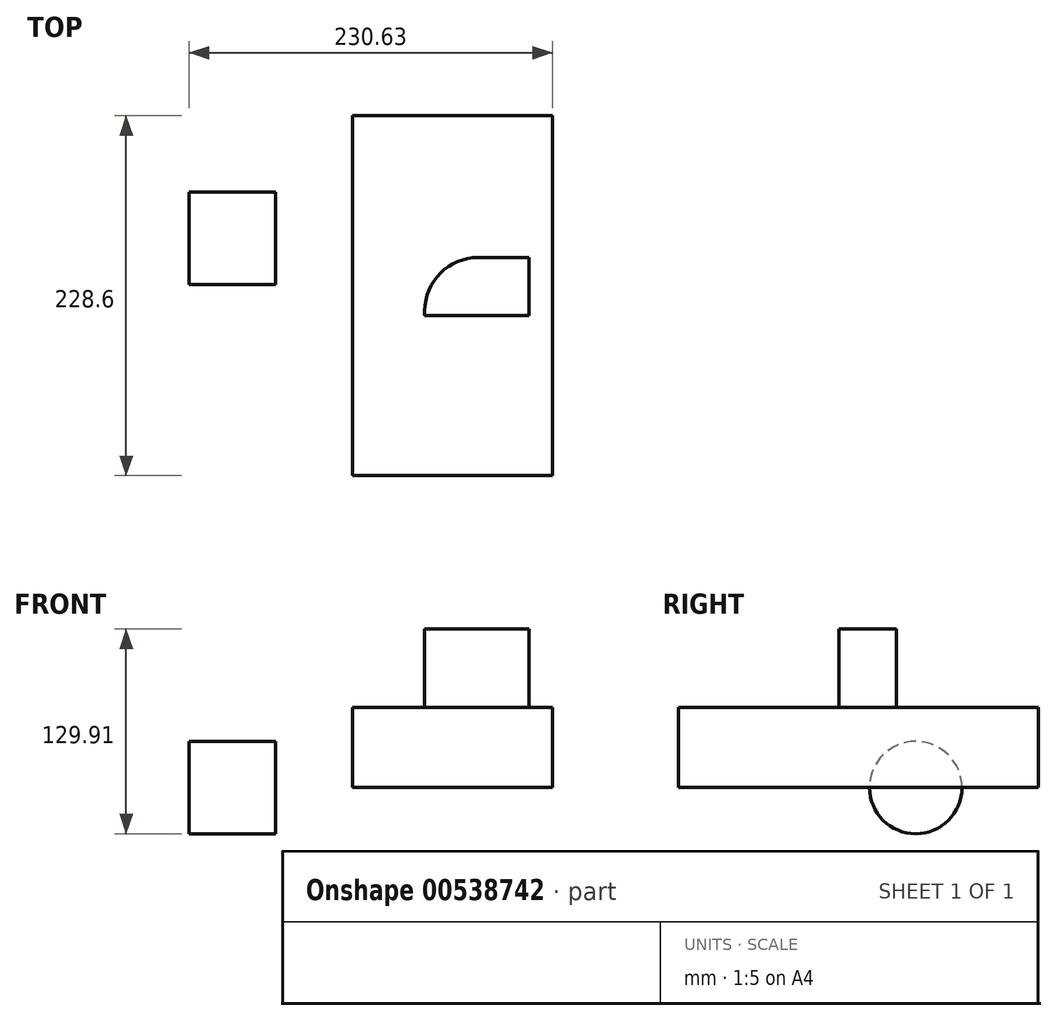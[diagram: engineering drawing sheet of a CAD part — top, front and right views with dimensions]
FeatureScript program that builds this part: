
annotation { "Feature Type Name" : "Feature", "Feature Type Description" : "" }
export const myFeature = defineFeature(function(context is Context, id is Id, definition is map)
    precondition{}
    {
        {
            var Q0;
            Q0=qCreatedBy(makeId("Top.planeOp"),FACE);
            var sketch = newSketch(context, id + "F0", { "sketchPlane" : qUnion([Q0])});
            skLineSegment(sketch, "E0.bottom", {"start": v(63.5, -114.3) * mm, "end": v(-63.5, -114.3) * mm});
            skLineSegment(sketch, "E0.top", {"start": v(63.5, 114.3) * mm, "end": v(-63.5, 114.3) * mm});
            skLineSegment(sketch, "E0.left", {"start": v(63.5, -114.3) * mm, "end": v(63.5, 114.3) * mm});
            skLineSegment(sketch, "E0.right", {"start": v(-63.5, -114.3) * mm, "end": v(-63.5, 114.3) * mm});
            skPoint(sketch, "E0.middle", {"position": v(0, 0) * mm});
            skSolve(sketch);
        }
        {
            var Q0;
            Q0 = qSketchRegion(id + "F0", true);
            extrude(context, id + "F1", {"entities" : qUnion([Q0]), "depth" : 50.8 * mm, "offsetDistance" : 25.4 * mm});
        }
        {
            var Q0;
            Q0=qCreatedBy(makeId("Top.planeOp"),FACE);
            var sketch = newSketch(context, id + "F2", { "sketchPlane" : qUnion([Q0])});
            skLineSegment(sketch, "E1.bottom", {"start": v(-141.73, 65.86) * mm, "end": v(-112.4, 65.86) * mm});
            skLineSegment(sketch, "E1.top", {"start": v(-141.73, 36.53) * mm, "end": v(-112.4, 36.53) * mm});
            skLineSegment(sketch, "E1.left", {"start": v(-141.73, 65.86) * mm, "end": v(-141.73, 36.53) * mm});
            skLineSegment(sketch, "E1.right", {"start": v(-112.4, 65.86) * mm, "end": v(-112.4, 36.53) * mm});
            skLineSegment(sketch, "E2", {"start": v(-141.73, 36.53) * mm, "end": v(-88.75, 36.53) * mm});
            skSolve(sketch);
        }
        {
            var Q0;
            Q0=makeQuery(id+"F2.imprint","IMPRINT",FACE,{"disambiguationData":[TD([[makeQuery(id+"F2.imprint","IMPRINT",EDGE,{"derivedFrom":sQuery(id+"F2.wireOp",EDGE,"E1.bottom")}),-1.0]])]});
            var Q1;
            Q1=sQuery(id+"F2.wireOp",EDGE,"E2");
            revolve(context, id + "F3", {"entities" : qUnion([Q0]), "axis" : qUnion([Q1]), "revolveType" : RevolveType.FULL});
        }
        {
            var Q0;
            Q0=makeQuery(id+"F3.opRevolve","SWEPT_FACE",FACE,{"disambiguationData":[OSD([sQuery(id+"F2.wireOp",EDGE,"E1.left")])]});
            extrude(context, id + "F4", {"entities" : qUnion([Q0]), "operationType" : NewBodyOperationType.ADD, "depth" : 25.4 * mm, "offsetDistance" : 25.4 * mm});
        }
        {
            var Q0;
            Q0=makeQuery(id+"F1.opExtrude","CAP_FACE",FACE,{"disambiguationData":[OSD([sQuery(id+"F0.wireOp",EDGE,"E0.bottom"),sQuery(id+"F0.wireOp",EDGE,"E0.top"),sQuery(id+"F0.wireOp",EDGE,"E0.left"),sQuery(id+"F0.wireOp",EDGE,"E0.right")])],"isStart":false});
            var sketch = newSketch(context, id + "F5", { "sketchPlane" : qUnion([Q0])});
            skLineSegment(sketch, "E3.bottom", {"start": v(16.45, 24.28) * mm, "end": v(48.75, 24.28) * mm});
            skLineSegment(sketch, "E3.top", {"start": v(-17.54, -12.41) * mm, "end": v(48.75, -12.41) * mm});
            skLineSegment(sketch, "E3.left", {"start": v(-17.54, -9.7) * mm, "end": v(-17.54, -12.41) * mm});
            skLineSegment(sketch, "E3.right", {"start": v(48.75, 24.28) * mm, "end": v(48.75, -12.41) * mm});
            skLineSegment(sketch, "E4.bottom", {"start": v(-17.54, -12.41) * mm, "end": v(-32.13, -12.41) * mm});
            skLineSegment(sketch, "E4.top", {"start": v(-17.54, -57.72) * mm, "end": v(-37.84, -57.72) * mm});
            skLineSegment(sketch, "E4.left", {"start": v(-17.54, -12.41) * mm, "end": v(-17.54, -57.72) * mm});
            skLineSegment(sketch, "E4.right", {"start": v(-37.84, -18.12) * mm, "end": v(-37.84, -57.72) * mm});
            skPoint(sketch, "E5.visualSharp", {"position": v(-17.54, 24.28) * mm});
            skArc(sketch, "E5.filletArc", {"start": v(16.45, 24.28) * mm, "mid": v(-7.58, 14.33) * mm, "end": v(-17.54, -9.7) * mm});
            skPoint(sketch, "E6.visualSharp", {"position": v(-37.84, -12.41) * mm});
            skArc(sketch, "E6.filletArc", {"start": v(-32.13, -12.41) * mm, "mid": v(-36.17, -14.09) * mm, "end": v(-37.84, -18.12) * mm});
            skArc(sketch, "E7", {"start": v(-41.78, 15.56) * mm, "mid": v(-12.37, 30.22) * mm, "end": v(-9.4, 62.95) * mm});
            skArc(sketch, "E8", {"start": v(-40.21, 49.24) * mm, "mid": v(-47.54, 19.8) * mm, "end": v(-17.54, 24.28) * mm});
            skSolve(sketch);
        }
        {
            var Q0;
            Q0=makeQuery(id+"F5.imprint","IMPRINT",FACE,{"disambiguationData":[TD([[makeQuery(id+"F5.imprint","IMPRINT",EDGE,{"derivedFrom":sQuery(id+"F5.wireOp",EDGE,"E3.bottom")}),-1.0]])]});
            extrude(context, id + "F6", {"entities" : qUnion([Q0]), "operationType" : NewBodyOperationType.ADD, "depth" : 49.78 * mm, "offsetDistance" : 25.4 * mm});
        }
    });
